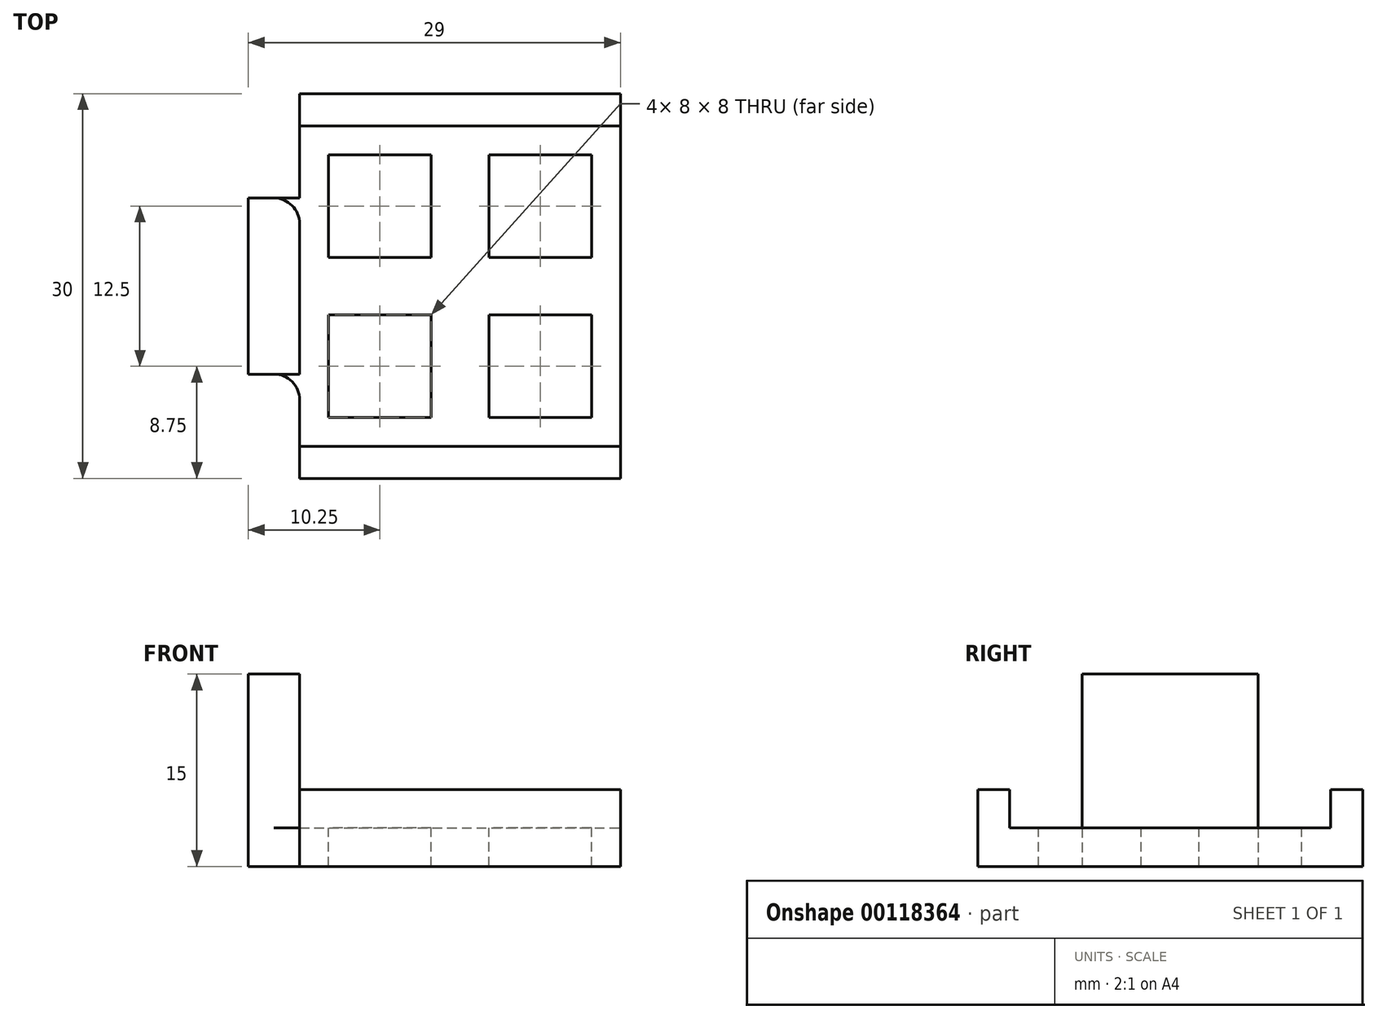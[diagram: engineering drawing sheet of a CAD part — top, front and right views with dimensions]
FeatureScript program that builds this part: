
annotation { "Feature Type Name" : "Feature", "Feature Type Description" : "" }
export const myFeature = defineFeature(function(context is Context, id is Id, definition is map)
    precondition{}
    {
        {
            var Q0;
            Q0=qCreatedBy(makeId("Top.planeOp"),FACE);
            var sketch = newSketch(context, id + "F0", { "sketchPlane" : qUnion([Q0])});
            skLineSegment(sketch, "E0.bottom", {"start": v(12.5, -15) * mm, "end": v(-12.5, -15) * mm});
            skLineSegment(sketch, "E0.top", {"start": v(12.5, 15) * mm, "end": v(-12.5, 15) * mm});
            skLineSegment(sketch, "E0.left", {"start": v(12.5, -15) * mm, "end": v(12.5, 15) * mm});
            skLineSegment(sketch, "E0.right", {"start": v(-12.5, -15) * mm, "end": v(-12.5, 15) * mm});
            skPoint(sketch, "E0.middle", {"position": v(0, 0) * mm});
            skSolve(sketch);
        }
        {
            var Q0;
            Q0=makeQuery(id+"F0.imprint","IMPRINT",FACE,{"disambiguationData":[TD([[makeQuery(id+"F0.imprint","IMPRINT",EDGE,{"derivedFrom":sQuery(id+"F0.wireOp",EDGE,"E0.bottom")}),-1.0]])]});
            extrude(context, id + "F1", {"entities" : qUnion([Q0]), "depth" : 3 * mm});
        }
        {
            var Q0;
            Q0=makeQuery(id+"F1.opExtrude","CAP_FACE",FACE,{"disambiguationData":[OSD([sQuery(id+"F0.wireOp",EDGE,"E0.bottom"),sQuery(id+"F0.wireOp",EDGE,"E0.top"),sQuery(id+"F0.wireOp",EDGE,"E0.left"),sQuery(id+"F0.wireOp",EDGE,"E0.right")])],"isStart":false});
            var sketch = newSketch(context, id + "F2", { "sketchPlane" : qUnion([Q0])});
            skLineSegment(sketch, "E1.bottom", {"start": v(-12.5, 15) * mm, "end": v(12.5, 15) * mm});
            skLineSegment(sketch, "E1.top", {"start": v(-12.5, 12.5) * mm, "end": v(12.5, 12.5) * mm});
            skLineSegment(sketch, "E1.left", {"start": v(-12.5, 15) * mm, "end": v(-12.5, 12.5) * mm});
            skLineSegment(sketch, "E1.right", {"start": v(12.5, 15) * mm, "end": v(12.5, 12.5) * mm});
            skLineSegment(sketch, "E2.bottom", {"start": v(-12.5, -15) * mm, "end": v(12.5, -15) * mm});
            skLineSegment(sketch, "E2.top", {"start": v(-12.5, -12.5) * mm, "end": v(12.5, -12.5) * mm});
            skLineSegment(sketch, "E2.left", {"start": v(-12.5, -15) * mm, "end": v(-12.5, -12.5) * mm});
            skLineSegment(sketch, "E2.right", {"start": v(12.5, -15) * mm, "end": v(12.5, -12.5) * mm});
            skSolve(sketch);
        }
        {
            var Q0;
            Q0 = qSketchRegion(id + "F2", true);
            extrude(context, id + "F3", {"entities" : qUnion([Q0]), "operationType" : NewBodyOperationType.ADD, "depth" : 3 * mm});
        }
        {
            var Q0;
            Q0=qCreatedBy(makeId("Top.planeOp"),FACE);
            var sketch = newSketch(context, id + "F4", { "sketchPlane" : qUnion([Q0])});
            skLineSegment(sketch, "E3.bottom", {"start": v(-12.5, -6.87) * mm, "end": v(-16.5, -6.87) * mm});
            skLineSegment(sketch, "E3.top", {"start": v(-12.5, 6.87) * mm, "end": v(-16.5, 6.87) * mm});
            skLineSegment(sketch, "E3.left", {"start": v(-12.5, -6.87) * mm, "end": v(-12.5, 6.87) * mm});
            skLineSegment(sketch, "E3.right", {"start": v(-16.5, -6.87) * mm, "end": v(-16.5, 6.87) * mm});
            skPoint(sketch, "E3.middle", {"position": v(-14.5, 0) * mm});
            skSolve(sketch);
        }
        {
            var Q0;
            Q0=makeQuery(id+"F4.imprint","IMPRINT",FACE,{"disambiguationData":[TD([[makeQuery(id+"F4.imprint","IMPRINT",EDGE,{"derivedFrom":sQuery(id+"F4.wireOp",EDGE,"E3.bottom")}),-1.0]])]});
            extrude(context, id + "F5", {"entities" : qUnion([Q0]), "operationType" : NewBodyOperationType.ADD, "depth" : 15 * mm});
        }
        {
            var Q0;
            {var subQ0=sQuery(id+"F4.wireOp",EDGE,"E3.bottom");Q0=makeQuery(id+"F5.boolean.opBoolean","SPLIT",EDGE,{"disambiguationData":[topologyDisambiguationEdgeConnected([makeQuery(id+"F1.opExtrude","SWEPT_FACE",FACE,{"disambiguationData":[OSD([sQuery(id+"F0.wireOp",EDGE,"E0.right")])]})])],"derivedFrom":makeQuery(id+"F5.opExtrude","SWEPT_EDGE",EDGE,{"disambiguationData":[OSD([subQ0,sQuery(id+"F4.wireOp",EDGE,"E3.left")])]})});}
            var Q1;
            {var subQ0=sQuery(id+"F4.wireOp",EDGE,"E3.top");Q1=makeQuery(id+"F5.boolean.opBoolean","SPLIT",EDGE,{"disambiguationData":[topologyDisambiguationEdgeConnected([makeQuery(id+"F1.opExtrude","SWEPT_FACE",FACE,{"disambiguationData":[OSD([sQuery(id+"F0.wireOp",EDGE,"E0.right")])]})])],"derivedFrom":makeQuery(id+"F5.opExtrude","SWEPT_EDGE",EDGE,{"disambiguationData":[OSD([subQ0,sQuery(id+"F4.wireOp",EDGE,"E3.left")])]})});}
            fillet(context, id + "F6", {"entities" : qUnion([Q0, Q1]), "radius" : 2 * mm, "tangentPropagation" : true, "allowEdgeOverflow" : false});
        }
        {
            var Q0;
            Q0=makeQuery(id+"F1.opExtrude","CAP_FACE",FACE,{"disambiguationData":[OSD([sQuery(id+"F0.wireOp",EDGE,"E0.bottom"),sQuery(id+"F0.wireOp",EDGE,"E0.top"),sQuery(id+"F0.wireOp",EDGE,"E0.left"),sQuery(id+"F0.wireOp",EDGE,"E0.right")])],"isStart":false});
            var sketch = newSketch(context, id + "F7", { "sketchPlane" : qUnion([Q0])});
            skLineSegment(sketch, "E4.bottom", {"start": v(6.25, -6.25) * mm, "end": v(-6.25, -6.25) * mm, "construction": true});
            skLineSegment(sketch, "E4.top", {"start": v(6.25, 6.25) * mm, "end": v(-6.25, 6.25) * mm, "construction": true});
            skLineSegment(sketch, "E4.left", {"start": v(6.25, -6.25) * mm, "end": v(6.25, 6.25) * mm, "construction": true});
            skLineSegment(sketch, "E4.right", {"start": v(-6.25, -6.25) * mm, "end": v(-6.25, 6.25) * mm, "construction": true});
            skPoint(sketch, "E4.middle", {"position": v(0, 0) * mm});
            skLineSegment(sketch, "E5.bottom", {"start": v(-2.25, 2.25) * mm, "end": v(-10.25, 2.25) * mm});
            skLineSegment(sketch, "E5.top", {"start": v(-2.25, 10.25) * mm, "end": v(-10.25, 10.25) * mm});
            skLineSegment(sketch, "E5.left", {"start": v(-2.25, 2.25) * mm, "end": v(-2.25, 10.25) * mm});
            skLineSegment(sketch, "E5.right", {"start": v(-10.25, 2.25) * mm, "end": v(-10.25, 10.25) * mm});
            skPoint(sketch, "E5.middle", {"position": v(-6.25, 6.25) * mm});
            skLineSegment(sketch, "E6.bottom", {"start": v(10.25, 2.25) * mm, "end": v(2.25, 2.25) * mm});
            skLineSegment(sketch, "E6.top", {"start": v(10.25, 10.25) * mm, "end": v(2.25, 10.25) * mm});
            skLineSegment(sketch, "E6.left", {"start": v(10.25, 2.25) * mm, "end": v(10.25, 10.25) * mm});
            skLineSegment(sketch, "E6.right", {"start": v(2.25, 2.25) * mm, "end": v(2.25, 10.25) * mm});
            skPoint(sketch, "E6.middle", {"position": v(6.25, 6.25) * mm});
            skLineSegment(sketch, "E7.bottom", {"start": v(-2.25, -10.25) * mm, "end": v(-10.25, -10.25) * mm});
            skLineSegment(sketch, "E7.top", {"start": v(-2.25, -2.25) * mm, "end": v(-10.25, -2.25) * mm});
            skLineSegment(sketch, "E7.left", {"start": v(-2.25, -10.25) * mm, "end": v(-2.25, -2.25) * mm});
            skLineSegment(sketch, "E7.right", {"start": v(-10.25, -10.25) * mm, "end": v(-10.25, -2.25) * mm});
            skPoint(sketch, "E7.middle", {"position": v(-6.25, -6.25) * mm});
            skLineSegment(sketch, "E8.bottom", {"start": v(10.25, -10.25) * mm, "end": v(2.25, -10.25) * mm});
            skLineSegment(sketch, "E8.top", {"start": v(10.25, -2.25) * mm, "end": v(2.25, -2.25) * mm});
            skLineSegment(sketch, "E8.left", {"start": v(10.25, -10.25) * mm, "end": v(10.25, -2.25) * mm});
            skLineSegment(sketch, "E8.right", {"start": v(2.25, -10.25) * mm, "end": v(2.25, -2.25) * mm});
            skPoint(sketch, "E8.middle", {"position": v(6.25, -6.25) * mm});
            skSolve(sketch);
        }
        {
            var Q0;
            Q0 = qSketchRegion(id + "F7", true);
            extrude(context, id + "F8", {"entities" : qUnion([Q0]), "operationType" : NewBodyOperationType.REMOVE, "oppositeDirection" : true, "depth" : 3 * mm});
        }
    });
